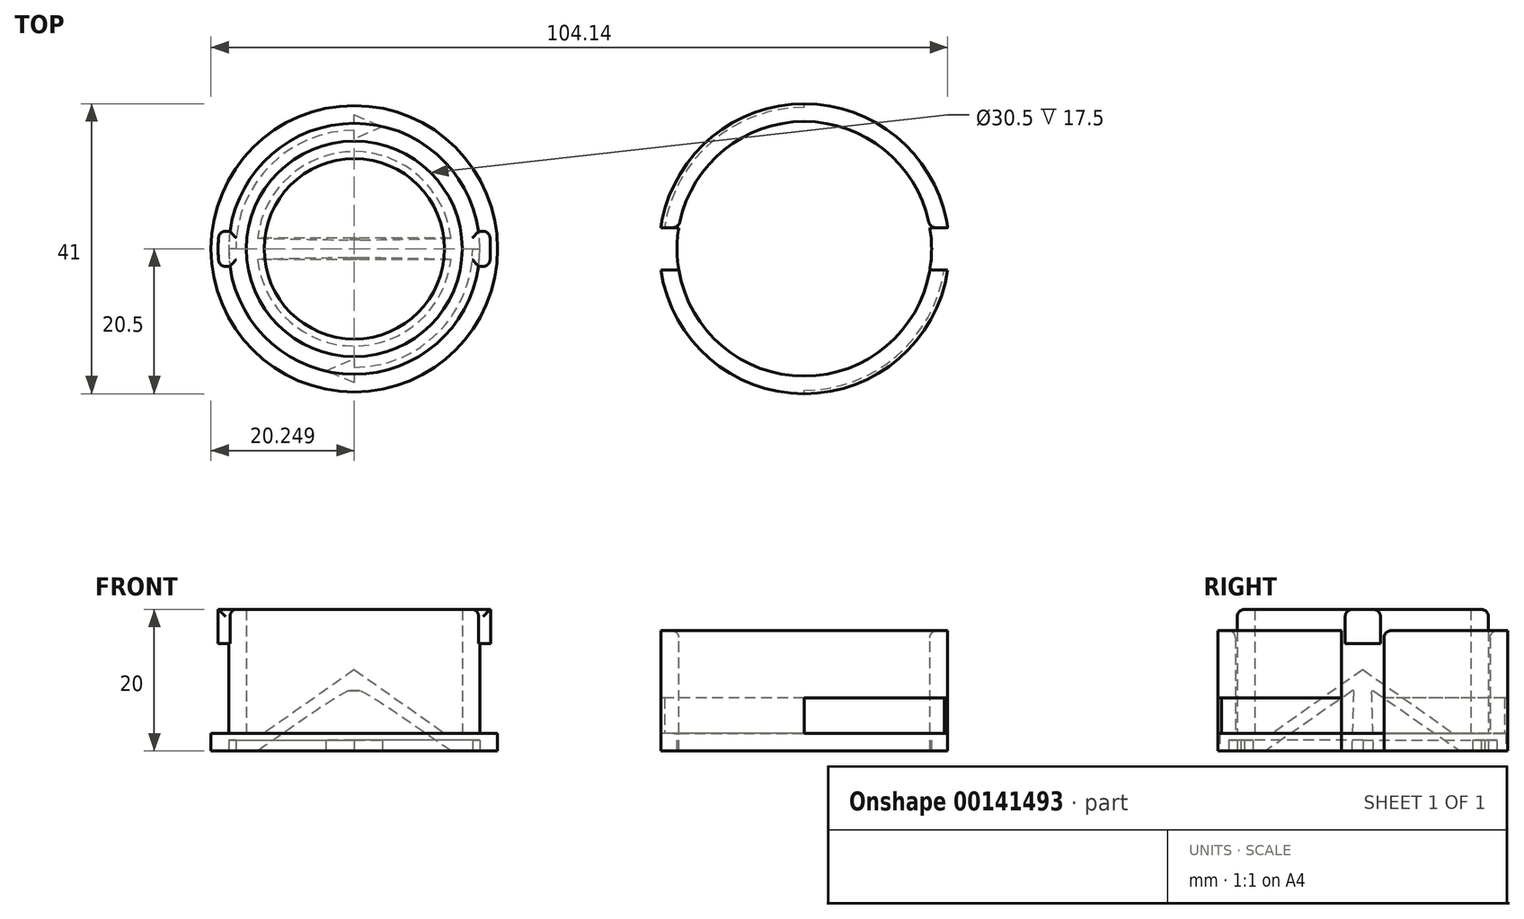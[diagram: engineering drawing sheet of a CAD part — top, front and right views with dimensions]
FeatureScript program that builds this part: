
annotation { "Feature Type Name" : "Feature", "Feature Type Description" : "" }
export const myFeature = defineFeature(function(context is Context, id is Id, definition is map)
    precondition{}
    {
        {
            var Q0;
            Q0=qCreatedBy(makeId("Top.planeOp"),FACE);
            var sketch = newSketch(context, id + "F0", { "sketchPlane" : qUnion([Q0])});
            skCircle(sketch, "E0", {"center": v(-80, 0) * mm, "radius": 20.5 * mm});
            skSolve(sketch);
        }
        {
            var Q0;
            Q0=makeQuery(id+"F0.imprint","IMPRINT",FACE,{"disambiguationData":[TD([[makeQuery(id+"F0.imprint","IMPRINT",EDGE,{"derivedFrom":sQuery(id+"F0.wireOp",EDGE,"E0")}),1.0]])]});
            extrude(context, id + "F1", {"entities" : qUnion([Q0]), "depth" : 17 * mm});
        }
        {
            var Q0;
            Q0=makeQuery(id+"F1.opExtrude","CAP_FACE",FACE,{"disambiguationData":[OSD([sQuery(id+"F0.wireOp",EDGE,"E0")])],"isStart":false});
            shell(context, id + "F2", {"entities" : qUnion([Q0]), "thickness" : 2.5 * mm});
        }
        {
            var Q0;
            Q0=makeQuery(id+"F1.opExtrude","CAP_FACE",FACE,{"disambiguationData":[OSD([sQuery(id+"F0.wireOp",EDGE,"E0")])],"isStart":false});
            var sketch = newSketch(context, id + "F3", { "sketchPlane" : qUnion([Q0])});
            skLineSegment(sketch, "E1.bottom", {"start": v(-104, -3) * mm, "end": v(-56, -3) * mm});
            skLineSegment(sketch, "E1.top", {"start": v(-104, 3) * mm, "end": v(-56, 3) * mm});
            skLineSegment(sketch, "E1.left", {"start": v(-104, -3) * mm, "end": v(-104, 3) * mm});
            skLineSegment(sketch, "E1.right", {"start": v(-56, -3) * mm, "end": v(-56, 3) * mm});
            skPoint(sketch, "E1.middle", {"position": v(-80, 0) * mm});
            skSolve(sketch);
        }
        {
            var Q0;
            {var subQ0=sQuery(id+"F3.wireOp",EDGE,"E1.bottom");var subQ1=sQuery(id+"F0.wireOp",EDGE,"E0");var subQ2=makeQuery(id+"F1.opExtrude","CAP_EDGE",EDGE,{"disambiguationData":[OSD([subQ1])],"isStart":false});var subQ3=makeQuery(id+"F3.imprint","INTERSECT",VERTEX,{"disambiguationData":[OD(1.0)],"derivedFrom":[subQ2,subQ0]});Q0=makeQuery(id+"F3.imprint","IMPRINT",FACE,{"disambiguationData":[TD([[makeQuery(id+"F3.imprint","IMPRINT",EDGE,{"disambiguationData":[TD([[subQ3,-1.0]])],"derivedFrom":subQ2}),1.0]])]});}
            var Q1;
            {var subQ0=sQuery(id+"F3.wireOp",EDGE,"E1.bottom");var subQ1=sQuery(id+"F0.wireOp",EDGE,"E0");var subQ2=makeQuery(id+"F1.opExtrude","CAP_EDGE",EDGE,{"disambiguationData":[OSD([subQ1])],"isStart":false});var subQ3=makeQuery(id+"F3.imprint","INTERSECT",VERTEX,{"disambiguationData":[OD(0.0)],"derivedFrom":[subQ2,subQ0]});Q1=makeQuery(id+"F3.imprint","IMPRINT",FACE,{"disambiguationData":[TD([[makeQuery(id+"F3.imprint","IMPRINT",EDGE,{"disambiguationData":[TD([[subQ3,1.0]])],"derivedFrom":subQ2}),1.0]])]});}
            extrude(context, id + "F4", {"entities" : qUnion([Q0, Q1]), "operationType" : NewBodyOperationType.REMOVE, "oppositeDirection" : true, "depth" : (19.5 - 2.5) * mm});
        }
        {
            var Q0;
            {var subQ0=sQuery(id+"F0.wireOp",EDGE,"E0");Q0=makeQuery(id+"F2.opShell","OFFSET_FACE",FACE,{"disambiguationData":[OSD([subQ0]),TDD([makeQuery(id+"F1.opExtrude","CAP_FACE",FACE,{"disambiguationData":[OSD([subQ0])],"isStart":true})])]});}
            var sketch = newSketch(context, id + "F5", { "sketchPlane" : qUnion([Q0])});
            skPoint(sketch, "E2.0.3.end.orphan", {"position": v(-59.72, 3) * mm});
            skPoint(sketch, "E2.0.3.start.orphan", {"position": v(-62.25, 3) * mm});
            skPoint(sketch, "E3.0.0.end.orphan", {"position": v(-100.28, -3) * mm});
            skPoint(sketch, "E3.0.0.start.orphan", {"position": v(-97.75, -3) * mm});
            skLineSegment(sketch, "E4", {"start": v(-80, 20) * mm, "end": v(-80, 33.67) * mm, "construction": true});
            skArc(sketch, "E5", {"start": v(-80, -20) * mm, "mid": v(-65.86, -14.14) * mm, "end": v(-60, 0) * mm});
            skArc(sketch, "E6.0", {"start": v(-80, -21.5) * mm, "mid": v(-64.8, -15.2) * mm, "end": v(-58.5, 0) * mm});
            skLineSegment(sketch, "E7", {"start": v(-80, -21.5) * mm, "end": v(-80, -20) * mm});
            skPoint(sketch, "E7.startSnap0", {"position": v(-80, -20) * mm});
            skLineSegment(sketch, "E8", {"start": v(-101.5, 0) * mm, "end": v(-100, 0) * mm});
            skPoint(sketch, "E9.orphan", {"position": v(-80, -26.36) * mm});
            skLineSegment(sketch, "E10.trimOffspring", {"start": v(-80, 0) * mm, "end": v(-80, 33.67) * mm});
            skArc(sketch, "E11.trimOffspring", {"start": v(-80, 21.5) * mm, "mid": v(-95.2, 15.2) * mm, "end": v(-101.5, 0) * mm});
            skArc(sketch, "E12.trimOffspring", {"start": v(-60.23, 3) * mm, "mid": v(-83, 19.77) * mm, "end": v(-99.77, -3) * mm});
            skLineSegment(sketch, "E13.trimOffspring", {"start": v(-60, 0) * mm, "end": v(-58.5, 0) * mm});
            skPoint(sketch, "E14.orphan", {"position": v(-104.22, 0) * mm});
            skSolve(sketch);
        }
        {
            var Q0;
            Q0=qSketchRegion(id+"F5",true);
            extrude(context, id + "F6", {"entities" : qUnion([Q0]), "depth" : 5 * mm});
        }
        {
            var Q0;
            Q0=makeQuery(id+"F6.opExtrude","SWEPT_BODY",BODY,{"disambiguationData":[OSD([sQuery(id+"F5.wireOp",EDGE,"E5"),sQuery(id+"F5.wireOp",EDGE,"E6.0"),sQuery(id+"F5.wireOp",EDGE,"E7"),sQuery(id+"F5.wireOp",EDGE,"E13.trimOffspring")])]});
            var Q1;
            Q1=makeQuery(id+"F6.opExtrude","SWEPT_BODY",BODY,{"disambiguationData":[OSD([sQuery(id+"F5.wireOp",EDGE,"E8"),sQuery(id+"F5.wireOp",EDGE,"E10.trimOffspring"),sQuery(id+"F5.wireOp",EDGE,"E11.trimOffspring"),sQuery(id+"F5.wireOp",EDGE,"E12.trimOffspring")])]});
            var Q2;
            Q2=makeQuery(id+"F1.opExtrude","SWEPT_BODY",BODY,{"disambiguationData":[OSD([sQuery(id+"F0.wireOp",EDGE,"E0")])]});
            booleanBodies(context, id + "F7", {"operationType" : BooleanOperationType.SUBTRACTION, "tools" : qUnion([Q0, Q1]), "targets" : qUnion([Q2])});
        }
        {
            var Q0;
            {var subQ0=sQuery(id+"F3.wireOp",EDGE,"E1.bottom");var subQ1=sQuery(id+"F0.wireOp",EDGE,"E0");var subQ2=makeQuery(id+"F1.opExtrude","CAP_EDGE",EDGE,{"disambiguationData":[OSD([subQ1])],"isStart":false});Q0=makeQuery(id+"F4.boolean.opBoolean","COPY",EDGE,{"derivedFrom":makeQuery(id+"F4.opExtrude","CAP_EDGE",EDGE,{"disambiguationData":[OSD([subQ0]),TDD([makeQuery(id+"F3.imprint","IMPRINT",EDGE,{"disambiguationData":[TD([[makeQuery(id+"F3.imprint","INTERSECT",VERTEX,{"disambiguationData":[OD(1.0)],"derivedFrom":[subQ2,subQ0]}),1.0]])],"derivedFrom":subQ0})])],"isStart":true})});}
            var Q1;
            {var subQ0=sQuery(id+"F3.wireOp",EDGE,"E1.top");var subQ1=sQuery(id+"F0.wireOp",EDGE,"E0");var subQ2=makeQuery(id+"F1.opExtrude","CAP_EDGE",EDGE,{"disambiguationData":[OSD([subQ1])],"isStart":false});Q1=makeQuery(id+"F4.boolean.opBoolean","COPY",EDGE,{"derivedFrom":makeQuery(id+"F4.opExtrude","CAP_EDGE",EDGE,{"disambiguationData":[OSD([subQ0]),TDD([makeQuery(id+"F3.imprint","IMPRINT",EDGE,{"disambiguationData":[TD([[makeQuery(id+"F3.imprint","INTERSECT",VERTEX,{"disambiguationData":[OD(1.0)],"derivedFrom":[subQ2,subQ0]}),1.0]])],"derivedFrom":subQ0})])],"isStart":true})});}
            var Q2;
            {var subQ0=sQuery(id+"F3.wireOp",EDGE,"E1.top");var subQ1=sQuery(id+"F0.wireOp",EDGE,"E0");var subQ2=makeQuery(id+"F1.opExtrude","CAP_EDGE",EDGE,{"disambiguationData":[OSD([subQ1])],"isStart":false});Q2=makeQuery(id+"F4.boolean.opBoolean","COPY",EDGE,{"derivedFrom":makeQuery(id+"F4.opExtrude","CAP_EDGE",EDGE,{"disambiguationData":[OSD([subQ0]),TDD([makeQuery(id+"F3.imprint","IMPRINT",EDGE,{"disambiguationData":[TD([[makeQuery(id+"F3.imprint","INTERSECT",VERTEX,{"disambiguationData":[OD(0.0)],"derivedFrom":[subQ2,subQ0]}),-1.0]])],"derivedFrom":subQ0})])],"isStart":true})});}
            var Q3;
            {var subQ0=sQuery(id+"F3.wireOp",EDGE,"E1.bottom");var subQ1=sQuery(id+"F0.wireOp",EDGE,"E0");var subQ2=makeQuery(id+"F1.opExtrude","CAP_EDGE",EDGE,{"disambiguationData":[OSD([subQ1])],"isStart":false});Q3=makeQuery(id+"F4.boolean.opBoolean","COPY",EDGE,{"derivedFrom":makeQuery(id+"F4.opExtrude","CAP_EDGE",EDGE,{"disambiguationData":[OSD([subQ0]),TDD([makeQuery(id+"F3.imprint","IMPRINT",EDGE,{"disambiguationData":[TD([[makeQuery(id+"F3.imprint","INTERSECT",VERTEX,{"disambiguationData":[OD(0.0)],"derivedFrom":[subQ2,subQ0]}),-1.0]])],"derivedFrom":subQ0})])],"isStart":true})});}
            var Q4;
            Q4=makeQuery(id+"F7.opBoolean","COPY",EDGE,{"derivedFrom":makeQuery(id+"F6.opExtrude","SWEPT_EDGE",EDGE,{"disambiguationData":[OSD([sQuery(id+"F3.wireOp",EDGE,"E1.bottom"),sQuery(id+"F5.wireOp",EDGE,"E3.0.2"),sQuery(id+"F5.wireOp",EDGE,"8e49e918-ef75-4ded-bb09-875d22dd2186.0")])]})});
            var Q5;
            Q5=makeQuery(id+"F7.opBoolean","COPY",EDGE,{"derivedFrom":makeQuery(id+"F6.opExtrude","SWEPT_EDGE",EDGE,{"disambiguationData":[OSD([sQuery(id+"F3.wireOp",EDGE,"E1.top"),sQuery(id+"F5.wireOp",EDGE,"E2.0.1"),sQuery(id+"F5.wireOp",EDGE,"d106be05-fb70-4d25-ad0a-85b562e4b930.0")])]})});
            fillet(context, id + "F8", {"entities" : qUnion([Q0, Q1, Q2, Q3, Q4, Q5]), "radius" : 1 * mm, "tangentPropagation" : true, "allowEdgeOverflow" : false});
        }
        {
            var Q0;
            {var subQ0=sQuery(id+"F0.wireOp",EDGE,"E0");var subQ1=sQuery(id+"F3.wireOp",EDGE,"E1.top");var subQ2=makeQuery(id+"F1.opExtrude","CAP_EDGE",EDGE,{"disambiguationData":[OSD([subQ0])],"isStart":false});var subQ3=makeQuery(id+"F2.opShell","OFFSET_EDGE",EDGE,{"disambiguationData":[OSD([subQ0]),TDD([subQ2])]});Q0=makeQuery(id+"F4.boolean.opBoolean","SPLIT",EDGE,{"disambiguationData":[TD([makeQuery(id+"F4.opExtrude","SWEPT_FACE",FACE,{"disambiguationData":[OSD([subQ1]),TDD([makeQuery(id+"F3.imprint","IMPRINT",EDGE,{"disambiguationData":[TD([[makeQuery(id+"F3.imprint","INTERSECT",VERTEX,{"disambiguationData":[OD(0.0)],"derivedFrom":[subQ2,subQ1]}),-1.0]])],"derivedFrom":subQ1})])]})])],"derivedFrom":subQ3});}
            var Q1;
            {var subQ0=sQuery(id+"F0.wireOp",EDGE,"E0");var subQ1=sQuery(id+"F3.wireOp",EDGE,"E1.bottom");var subQ2=makeQuery(id+"F1.opExtrude","CAP_EDGE",EDGE,{"disambiguationData":[OSD([subQ0])],"isStart":false});var subQ3=makeQuery(id+"F2.opShell","OFFSET_EDGE",EDGE,{"disambiguationData":[OSD([subQ0]),TDD([subQ2])]});Q1=makeQuery(id+"F4.boolean.opBoolean","SPLIT",EDGE,{"disambiguationData":[TD([makeQuery(id+"F4.opExtrude","SWEPT_FACE",FACE,{"disambiguationData":[OSD([subQ1]),TDD([makeQuery(id+"F3.imprint","IMPRINT",EDGE,{"disambiguationData":[TD([[makeQuery(id+"F3.imprint","INTERSECT",VERTEX,{"disambiguationData":[OD(0.0)],"derivedFrom":[subQ2,subQ1]}),-1.0]])],"derivedFrom":subQ1})])]})])],"derivedFrom":subQ3});}
            fillet(context, id + "F9", {"entities" : qUnion([Q0, Q1]), "radius" : 1 * mm, "tangentPropagation" : true, "allowEdgeOverflow" : false});
        }
        {
            var Q0;
            Q0=qCreatedBy(makeId("Front.planeOp"),FACE);
            var sketch = newSketch(context, id + "F10", { "sketchPlane" : qUnion([Q0])});
            skLineSegment(sketch, "E15", {"start": v(-123.36, 0) * mm, "end": v(-163.86, 0) * mm, "construction": true});
            skLineSegment(sketch, "E16", {"start": v(-123.36, 0) * mm, "end": v(-129.86, 0) * mm});
            skPoint(sketch, "E17.endSnap0", {"position": v(-143.61, 0) * mm});
            skLineSegment(sketch, "E18", {"start": v(-143.61, 8.5) * mm, "end": v(-143.61, 11.5) * mm});
            skLineSegment(sketch, "E19", {"start": v(-143.61, 11.5) * mm, "end": v(-130.86, 2.5) * mm});
            skLineSegment(sketch, "E20", {"start": v(-130.86, 2.5) * mm, "end": v(-128.36, 2.5) * mm});
            skLineSegment(sketch, "E21", {"start": v(-128.36, 2.5) * mm, "end": v(-128.36, 20) * mm});
            skLineSegment(sketch, "E22", {"start": v(-128.36, 20) * mm, "end": v(-125.86, 20) * mm});
            skLineSegment(sketch, "E23", {"start": v(-125.86, 20) * mm, "end": v(-125.86, 2.5) * mm});
            skLineSegment(sketch, "E24", {"start": v(-125.86, 2.5) * mm, "end": v(-123.36, 2.5) * mm});
            skLineSegment(sketch, "E25", {"start": v(-123.36, 2.5) * mm, "end": v(-123.36, 0) * mm});
            skLineSegment(sketch, "E26", {"start": v(-143.61, 8.5) * mm, "end": v(-142.11, 8.5) * mm});
            skLineSegment(sketch, "E27", {"start": v(-142.11, 8.5) * mm, "end": v(-129.86, 0) * mm});
            skSolve(sketch);
        }
        {
            var Q0;
            Q0=makeQuery(id+"F10.imprint","IMPRINT",FACE,{"disambiguationData":[TD([[makeQuery(id+"F10.imprint","IMPRINT",EDGE,{"derivedFrom":sQuery(id+"F10.wireOp",EDGE,"E16")}),-1.0]])]});
            var Q1;
            Q1=sQuery(id+"F10.wireOp",EDGE,"E18");
            revolve(context, id + "F11", {"entities" : qUnion([Q0]), "axis" : qUnion([Q1]), "revolveType" : RevolveType.FULL});
        }
        {
            var Q0;
            Q0=makeQuery(id+"F11.opRevolve","SWEPT_FACE",FACE,{"disambiguationData":[OSD([sQuery(id+"F10.wireOp",EDGE,"E16")])]});
            var sketch = newSketch(context, id + "F12", { "sketchPlane" : qUnion([Q0])});
            skCircle(sketch, "E28.0", {"center": v(-143.61, 0) * mm, "radius": 17.75 * mm, "construction": true});
            skLineSegment(sketch, "E29.bottom", {"start": v(-127.61, -1.5) * mm, "end": v(-159.61, -1.5) * mm});
            skLineSegment(sketch, "E29.top", {"start": v(-127.61, 1.5) * mm, "end": v(-159.61, 1.5) * mm});
            skLineSegment(sketch, "E29.left", {"start": v(-127.61, -1.5) * mm, "end": v(-127.61, 1.5) * mm});
            skLineSegment(sketch, "E29.right", {"start": v(-159.61, -1.5) * mm, "end": v(-159.61, 1.5) * mm});
            skSolve(sketch);
        }
        {
            var Q0;
            Q0=makeQuery(id+"F11.opRevolve","SWEPT_FACE",FACE,{"disambiguationData":[OSD([sQuery(id+"F10.wireOp",EDGE,"E22")])]});
            var sketch = newSketch(context, id + "F13", { "sketchPlane" : qUnion([Q0])});
            skCircle(sketch, "E30.0", {"center": v(-143.61, 0) * mm, "radius": 17.75 * mm});
            skLineSegment(sketch, "E31.bottom", {"start": v(-162.7, 2.5) * mm, "end": v(-161.18, 2.5) * mm});
            skLineSegment(sketch, "E31.top", {"start": v(-162.7, -2.5) * mm, "end": v(-161.18, -2.5) * mm});
            skArc(sketch, "E32.0", {"start": v(-124.52, -2.5) * mm, "mid": v(-124.36, 0) * mm, "end": v(-124.52, 2.5) * mm});
            skPoint(sketch, "E31.left.end.orphan", {"position": v(-165.97, -2.5) * mm});
            skPoint(sketch, "E33.orphan", {"position": v(-165.97, 2.5) * mm});
            skArc(sketch, "E34.trimOffspring", {"start": v(-162.7, 2.5) * mm, "mid": v(-162.86, 0) * mm, "end": v(-162.7, -2.5) * mm});
            skLineSegment(sketch, "E35.trimOffspring", {"start": v(-126.04, 2.5) * mm, "end": v(-124.52, 2.5) * mm});
            skLineSegment(sketch, "E36.trimOffspring", {"start": v(-126.04, -2.5) * mm, "end": v(-124.52, -2.5) * mm});
            skPoint(sketch, "E31.right.start.orphan", {"position": v(-121.25, 2.5) * mm});
            skPoint(sketch, "E37.orphan", {"position": v(-121.25, -2.5) * mm});
            skSolve(sketch);
        }
        {
            var Q0;
            Q0=makeQuery(id+"F13.imprint","IMPRINT",FACE,{"disambiguationData":[TD([[makeQuery(id+"F13.imprint","IMPRINT",EDGE,{"derivedFrom":sQuery(id+"F13.wireOp",EDGE,"E32.0")}),1.0]])]});
            var Q1;
            {var subQ0=sQuery(id+"F13.wireOp",EDGE,"E31.bottom");Q1=makeQuery(id+"F13.imprint","IMPRINT",FACE,{"disambiguationData":[TD([[makeQuery(id+"F13.imprint","IMPRINT",EDGE,{"derivedFrom":subQ0}),-1.0]])]});}
            extrude(context, id + "F14", {"entities" : qUnion([Q0, Q1]), "operationType" : NewBodyOperationType.ADD, "oppositeDirection" : true, "depth" : 4.8 * mm});
        }
        {
            var Q0;
            {var subQ0=sQuery(id+"F13.wireOp",EDGE,"E31.bottom");var subQ3=sQuery(id+"F10.wireOp",EDGE,"E23");var subQ4=sQuery(id+"F10.wireOp",EDGE,"E22");Q0=makeQuery(id+"F14.boolean.opBoolean","SPLIT",EDGE,{"disambiguationData":[TD([makeQuery(id+"F14.opExtrude","SWEPT_FACE",FACE,{"disambiguationData":[OSD([subQ0])]})])],"derivedFrom":makeQuery(id+"F11.opRevolve","SWEPT_EDGE",EDGE,{"disambiguationData":[OSD([subQ4,subQ3])]})});}
            var Q1;
            {var subQ0=sQuery(id+"F13.wireOp",EDGE,"E31.top");var subQ3=sQuery(id+"F10.wireOp",EDGE,"E23");var subQ4=sQuery(id+"F10.wireOp",EDGE,"E22");Q1=makeQuery(id+"F14.boolean.opBoolean","SPLIT",EDGE,{"disambiguationData":[TD([makeQuery(id+"F14.opExtrude","SWEPT_FACE",FACE,{"disambiguationData":[OSD([subQ0])]})])],"derivedFrom":makeQuery(id+"F11.opRevolve","SWEPT_EDGE",EDGE,{"disambiguationData":[OSD([subQ4,subQ3])]})});}
            var Q2;
            Q2=makeQuery(id+"F14.opExtrude","CAP_EDGE",EDGE,{"disambiguationData":[OSD([sQuery(id+"F13.wireOp",EDGE,"E35.trimOffspring")])],"isStart":true});
            var Q3;
            Q3=makeQuery(id+"F14.opExtrude","CAP_EDGE",EDGE,{"disambiguationData":[OSD([sQuery(id+"F13.wireOp",EDGE,"E36.trimOffspring")])],"isStart":true});
            var Q4;
            Q4=makeQuery(id+"F14.opExtrude","CAP_EDGE",EDGE,{"disambiguationData":[OSD([sQuery(id+"F13.wireOp",EDGE,"E31.bottom")])],"isStart":true});
            var Q5;
            Q5=makeQuery(id+"F14.opExtrude","CAP_EDGE",EDGE,{"disambiguationData":[OSD([sQuery(id+"F13.wireOp",EDGE,"E31.top")])],"isStart":true});
            var Q6;
            Q6=makeQuery(id+"F14.opExtrude","SWEPT_EDGE",EDGE,{"disambiguationData":[OSD([sQuery(id+"F13.wireOp",EDGE,"E31.bottom"),sQuery(id+"F13.wireOp",EDGE,"E34.trimOffspring")])]});
            var Q7;
            Q7=makeQuery(id+"F14.opExtrude","SWEPT_EDGE",EDGE,{"disambiguationData":[OSD([sQuery(id+"F13.wireOp",EDGE,"E31.top"),sQuery(id+"F13.wireOp",EDGE,"E34.trimOffspring")])]});
            var Q8;
            Q8=makeQuery(id+"F14.opExtrude","SWEPT_EDGE",EDGE,{"disambiguationData":[OSD([sQuery(id+"F13.wireOp",EDGE,"E32.0"),sQuery(id+"F13.wireOp",EDGE,"E36.trimOffspring")])]});
            var Q9;
            Q9=makeQuery(id+"F14.opExtrude","SWEPT_EDGE",EDGE,{"disambiguationData":[OSD([sQuery(id+"F13.wireOp",EDGE,"E32.0"),sQuery(id+"F13.wireOp",EDGE,"E35.trimOffspring")])]});
            fillet(context, id + "F15", {"entities" : qUnion([Q0, Q1, Q2, Q3, Q4, Q5, Q6, Q7, Q8, Q9]), "radius" : 1 * mm, "tangentPropagation" : true, "allowEdgeOverflow" : false});
        }
        {
            var Q0;
            {var subQ0=sQuery(id+"F10.wireOp",EDGE,"E16");Q0=makeQuery(id+"F9nA7cOrPAyuwMp_5.boolean.opBoolean","MERGE",FACE,{"derivedFrom":[makeQuery(id+"F11.opRevolve","SWEPT_FACE",FACE,{"disambiguationData":[OSD([subQ0])]}),makeQuery(id+"F9nA7cOrPAyuwMp_5.opExtrude","CAP_FACE",FACE,{"disambiguationData":[OSD([subQ0,sQuery(id+"F10.wireOp",EDGE,"E17"),sQuery(id+"F12.wireOp",EDGE,"E29.bottom"),sQuery(id+"F12.wireOp",EDGE,"E29.top")])],"isStart":true})]});}
            var sketch = newSketch(context, id + "F16", { "sketchPlane" : qUnion([Q0])});
            skCircle(sketch, "E38.0", {"center": v(-143.61, 0) * mm, "radius": 20.25 * mm});
            skArc(sketch, "E39.0", {"start": v(-161.36, 0) * mm, "mid": v(-156.16, -12.55) * mm, "end": v(-143.61, -17.75) * mm});
            skArc(sketch, "E40.0", {"start": v(-160.36, 0) * mm, "mid": v(-155.45, -11.84) * mm, "end": v(-143.61, -16.75) * mm});
            skLineSegment(sketch, "E41", {"start": v(-160.36, 0) * mm, "end": v(-161.36, 0) * mm});
            skLineSegment(sketch, "E42", {"start": v(-143.61, -17.75) * mm, "end": v(-143.61, -18.95) * mm});
            skLineSegment(sketch, "E43", {"start": v(-143.61, -18.95) * mm, "end": v(-139.61, -17.25) * mm});
            skLineSegment(sketch, "E44", {"start": v(-139.61, -17.25) * mm, "end": v(-143.61, -15.55) * mm});
            skLineSegment(sketch, "E45", {"start": v(-143.61, -15.55) * mm, "end": v(-143.61, -16.75) * mm});
            skLineSegment(sketch, "E46", {"start": v(-143.61, 0) * mm, "end": v(-143.61, -20.25) * mm, "construction": true});
            skSolve(sketch);
        }
        {
            var Q0;
            Q0=makeQuery(id+"F16.imprint","IMPRINT",FACE,{"disambiguationData":[TD([[makeQuery(id+"F16.imprint","IMPRINT",EDGE,{"derivedFrom":sQuery(id+"F16.wireOp",EDGE,"E39.0")}),1.0]])]});
            extrude(context, id + "F17", {"entities" : qUnion([Q0]), "oppositeDirection" : true, "depth" : 1.5 * mm});
        }
        {
            var Q0;
            Q0=makeQuery(id+"F17.opExtrude","SWEPT_BODY",BODY,{"disambiguationData":[OSD([sQuery(id+"F16.wireOp",EDGE,"E39.0"),sQuery(id+"F16.wireOp",EDGE,"E40.0"),sQuery(id+"F16.wireOp",EDGE,"E41"),sQuery(id+"F16.wireOp",EDGE,"E42"),sQuery(id+"F16.wireOp",EDGE,"E43"),sQuery(id+"F16.wireOp",EDGE,"E44"),sQuery(id+"F16.wireOp",EDGE,"E45")])]});
            var Q1;
            Q1=makeQuery(id+"F11.opRevolve","SWEPT_EDGE",EDGE,{"disambiguationData":[OSD([sQuery(id+"F10.wireOp",EDGE,"E16"),sQuery(id+"F10.wireOp",EDGE,"E25")])]});
            circularPattern(context, id + "F18", {"entities" : qUnion([Q0]), "axis" : qUnion([Q1]), "angle" : 180 * degree, "instanceCount" : 2});
        }
        {
            var Q0;
            Q0=makeQuery(id+"F18.opPattern","COPY",BODY,{"derivedFrom":makeQuery(id+"F17.opExtrude","SWEPT_BODY",BODY,{"disambiguationData":[OSD([sQuery(id+"F16.wireOp",EDGE,"E39.0"),sQuery(id+"F16.wireOp",EDGE,"E40.0"),sQuery(id+"F16.wireOp",EDGE,"E41"),sQuery(id+"F16.wireOp",EDGE,"E42"),sQuery(id+"F16.wireOp",EDGE,"E43"),sQuery(id+"F16.wireOp",EDGE,"E44"),sQuery(id+"F16.wireOp",EDGE,"E45")])]}),"instanceName":"1"});
            var Q1;
            Q1=makeQuery(id+"F17.opExtrude","SWEPT_BODY",BODY,{"disambiguationData":[OSD([sQuery(id+"F16.wireOp",EDGE,"E39.0"),sQuery(id+"F16.wireOp",EDGE,"E40.0"),sQuery(id+"F16.wireOp",EDGE,"E41"),sQuery(id+"F16.wireOp",EDGE,"E42"),sQuery(id+"F16.wireOp",EDGE,"E43"),sQuery(id+"F16.wireOp",EDGE,"E44"),sQuery(id+"F16.wireOp",EDGE,"E45")])]});
            var Q2;
            Q2=makeQuery(id+"F11.opRevolve","SWEPT_BODY",BODY,{"disambiguationData":[OSD([sQuery(id+"F10.wireOp",EDGE,"E16"),sQuery(id+"F10.wireOp",EDGE,"E17"),sQuery(id+"F10.wireOp",EDGE,"E18"),sQuery(id+"F10.wireOp",EDGE,"E19"),sQuery(id+"F10.wireOp",EDGE,"E20"),sQuery(id+"F10.wireOp",EDGE,"E21"),sQuery(id+"F10.wireOp",EDGE,"E22"),sQuery(id+"F10.wireOp",EDGE,"E23"),sQuery(id+"F10.wireOp",EDGE,"E24"),sQuery(id+"F10.wireOp",EDGE,"E25")])]});
            booleanBodies(context, id + "F19", {"operationType" : BooleanOperationType.SUBTRACTION, "tools" : qUnion([Q0, Q1]), "targets" : qUnion([Q2])});
        }
        {
            var Q0;
            Q0=makeQuery(id+"F11.opRevolve","SWEPT_FACE",FACE,{"disambiguationData":[OSD([sQuery(id+"F10.wireOp",EDGE,"E26")])]});
            var sketch = newSketch(context, id + "F20", { "sketchPlane" : qUnion([Q0])});
            skLineSegment(sketch, "E47.bottom", {"start": v(-141.11, 1.25) * mm, "end": v(-146.11, 1.25) * mm});
            skLineSegment(sketch, "E47.top", {"start": v(-141.11, -1.25) * mm, "end": v(-146.11, -1.25) * mm});
            skLineSegment(sketch, "E47.left", {"start": v(-141.11, 1.25) * mm, "end": v(-141.11, -1.25) * mm});
            skLineSegment(sketch, "E47.right", {"start": v(-146.11, 1.25) * mm, "end": v(-146.11, -1.25) * mm});
            skPoint(sketch, "E47.middle", {"position": v(-143.61, 0) * mm});
            skSolve(sketch);
        }
        {
            var Q1;
            Q1 = qSketchRegion(id + "F20", true);
            var Q2;
            Q2 = qSketchRegion(id + "F12", true);
            loft(context, id + "F21", {"operationType" : NewBodyOperationType.ADD, "sheetProfilesArray" : [{ "sheetProfileEntities" : qUnion([Q1]) }, { "sheetProfileEntities" : qUnion([Q2]) }]});
        }
    });
